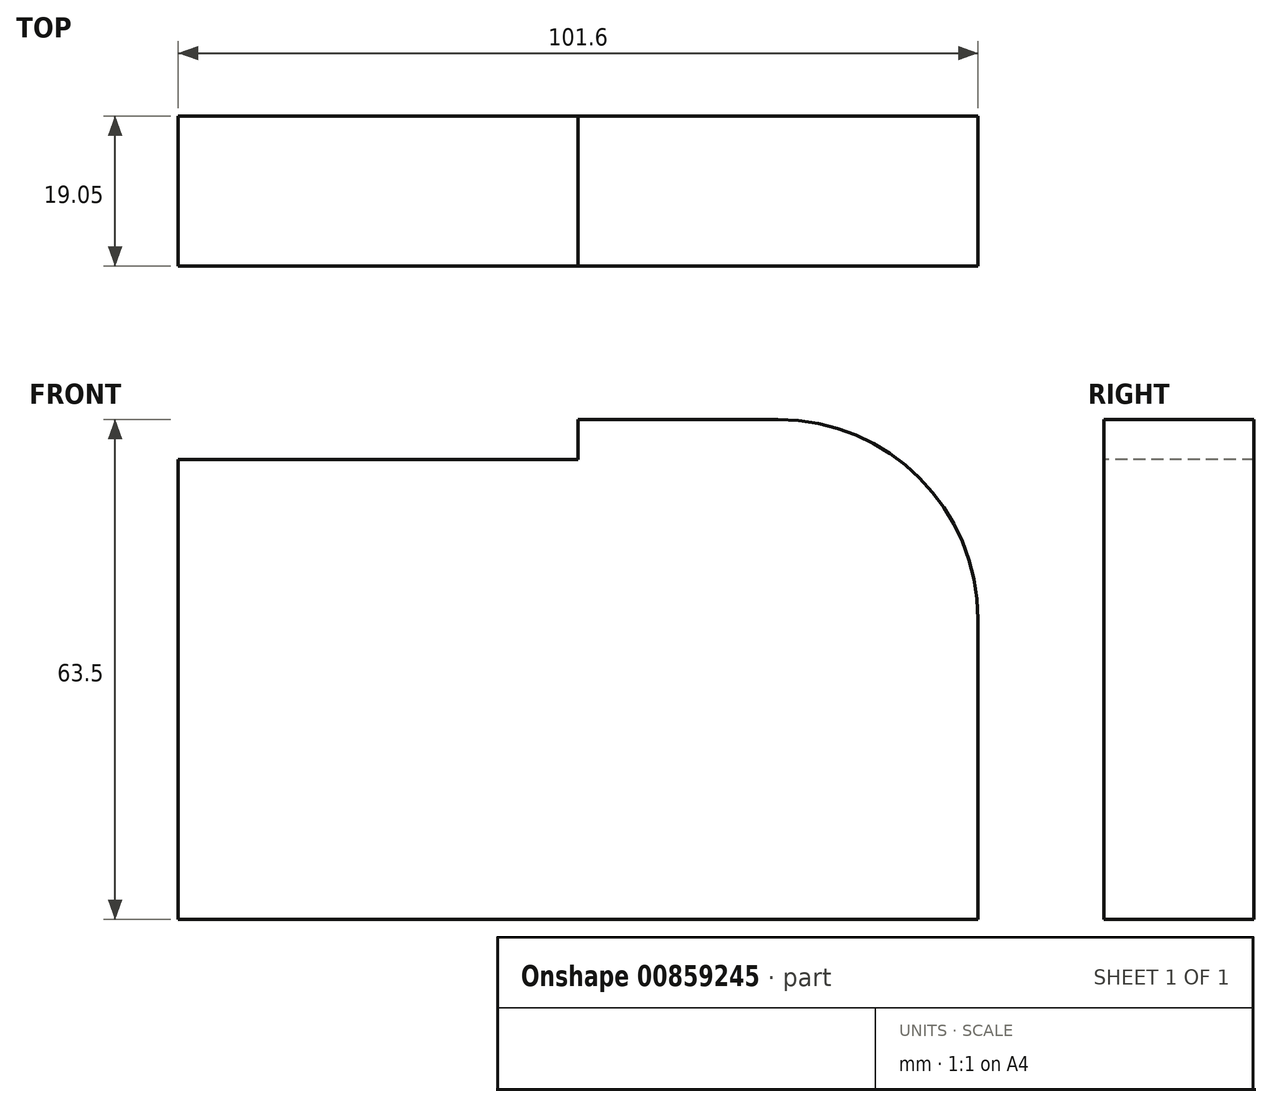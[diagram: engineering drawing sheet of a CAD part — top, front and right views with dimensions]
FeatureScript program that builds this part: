
annotation { "Feature Type Name" : "Feature", "Feature Type Description" : "" }
export const myFeature = defineFeature(function(context is Context, id is Id, definition is map)
    precondition{}
    {
        {
            var Q0;
            Q0=qCreatedBy(makeId("Front.planeOp"),FACE);
            var sketch = newSketch(context, id + "F0", { "sketchPlane" : qUnion([Q0])});
            skLineSegment(sketch, "E0.bottom", {"start": v(0, 0) * mm, "end": v(101.6, 0) * mm});
            skLineSegment(sketch, "E0.top", {"start": v(0, 63.5) * mm, "end": v(76.2, 63.5) * mm});
            skLineSegment(sketch, "E0.left", {"start": v(0, 0) * mm, "end": v(0, 63.5) * mm});
            skLineSegment(sketch, "E0.right", {"start": v(101.6, 0) * mm, "end": v(101.6, 38.1) * mm});
            skArc(sketch, "E1", {"start": v(101.6, 38.1) * mm, "mid": v(94.16, 56.06) * mm, "end": v(76.2, 63.5) * mm});
            skSolve(sketch);
        }
        {
            var Q0;
            Q0=makeQuery(id+"F0.imprint","IMPRINT",FACE,{"disambiguationData":[TD([[makeQuery(id+"F0.imprint","IMPRINT",EDGE,{"derivedFrom":sQuery(id+"F0.wireOp",EDGE,"E0.bottom")}),1.0]])]});
            extrude(context, id + "F1", {"entities" : qUnion([Q0]), "depth" : 19.05 * mm, "offsetDistance" : 25.4 * mm});
        }
        {
            var Q0;
            Q0=makeQuery(id+"F1.opExtrude","CAP_FACE",FACE,{"disambiguationData":[OSD([sQuery(id+"F0.wireOp",EDGE,"E0.bottom"),sQuery(id+"F0.wireOp",EDGE,"E0.top"),sQuery(id+"F0.wireOp",EDGE,"E0.left"),sQuery(id+"F0.wireOp",EDGE,"E0.right"),sQuery(id+"F0.wireOp",EDGE,"E1")])],"isStart":false});
            var sketch = newSketch(context, id + "F2", { "sketchPlane" : qUnion([Q0])});
            skLineSegment(sketch, "E2.bottom", {"start": v(0, 63.5) * mm, "end": v(50.8, 63.5) * mm});
            skLineSegment(sketch, "E2.top", {"start": v(0, 58.42) * mm, "end": v(50.8, 58.42) * mm});
            skLineSegment(sketch, "E2.left", {"start": v(0, 63.5) * mm, "end": v(0, 58.42) * mm});
            skLineSegment(sketch, "E2.right", {"start": v(50.8, 63.5) * mm, "end": v(50.8, 58.42) * mm});
            skSolve(sketch);
        }
        {
            var Q0;
            Q0=makeQuery(id+"F2.imprint","IMPRINT",FACE,{"disambiguationData":[TD([[makeQuery(id+"F2.imprint","IMPRINT",EDGE,{"derivedFrom":sQuery(id+"F2.wireOp",EDGE,"E2.bottom")}),-1.0]])]});
            extrude(context, id + "F3", {"entities" : qUnion([Q0]), "operationType" : NewBodyOperationType.REMOVE, "oppositeDirection" : true, "depth" : 19.05 * mm, "offsetDistance" : 25.4 * mm});
        }
    });
